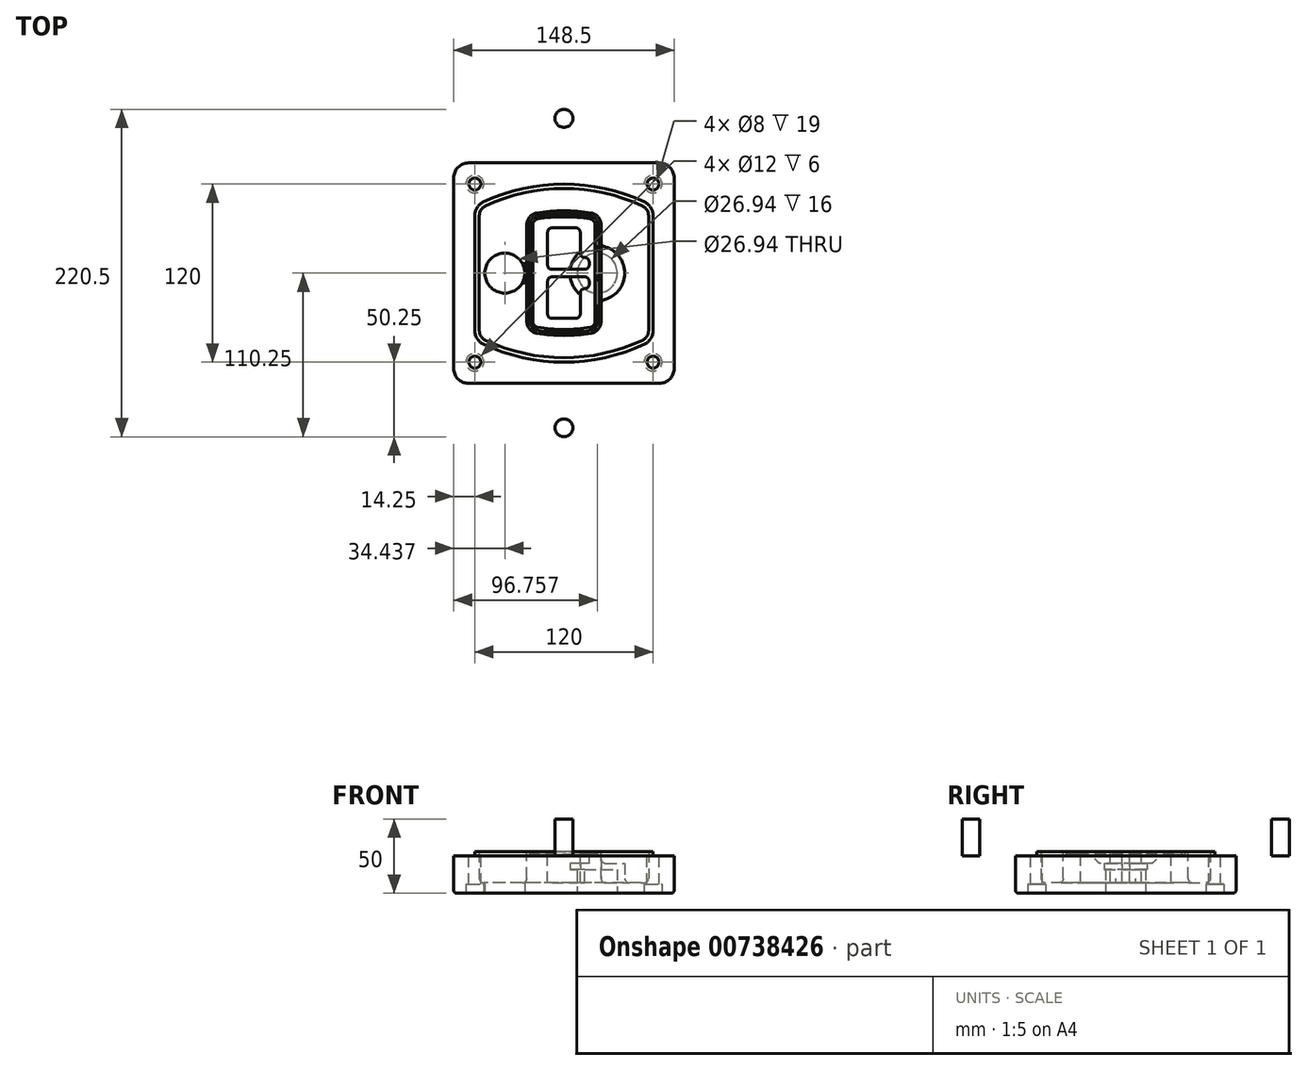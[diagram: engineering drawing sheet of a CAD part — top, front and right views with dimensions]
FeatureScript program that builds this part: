
annotation { "Feature Type Name" : "Feature", "Feature Type Description" : "" }
export const myFeature = defineFeature(function(context is Context, id is Id, definition is map)
    precondition{}
    {
        {
            var Q0;
            Q0=qCreatedBy(makeId("Top.planeOp"),FACE);
            var sketch = newSketch(context, id + "F0", { "sketchPlane" : qUnion([Q0])});
            skPoint(sketch, "E0.rect.middle", {"position": v(0, 0) * mm});
            skLineSegment(sketch, "E1.bottom", {"start": v(-64.25, -74.25) * mm, "end": v(64.25, -74.25) * mm});
            skLineSegment(sketch, "E1.top", {"start": v(-64.25, 74.25) * mm, "end": v(64.25, 74.25) * mm});
            skLineSegment(sketch, "E1.left", {"start": v(-74.25, -64.25) * mm, "end": v(-74.25, 64.25) * mm});
            skLineSegment(sketch, "E1.right", {"start": v(74.25, -64.25) * mm, "end": v(74.25, 64.25) * mm});
            skLineSegment(sketch, "E2", {"start": v(-74.25, 74.25) * mm, "end": v(74.25, -74.25) * mm, "construction": true});
            skLineSegment(sketch, "E3", {"start": v(74.25, 74.25) * mm, "end": v(-74.25, -74.25) * mm, "construction": true});
            skCircle(sketch, "E4", {"center": v(-60, 60) * mm, "radius": 4 * mm});
            skCircle(sketch, "E5", {"center": v(60, 60) * mm, "radius": 4 * mm});
            skCircle(sketch, "E6", {"center": v(60, -60) * mm, "radius": 4 * mm});
            skCircle(sketch, "E7", {"center": v(-60, -60) * mm, "radius": 4 * mm});
            skLineSegment(sketch, "E8", {"start": v(-60, 60) * mm, "end": v(60, 60) * mm, "construction": true});
            skLineSegment(sketch, "E9", {"start": v(60, 60) * mm, "end": v(60, -60) * mm, "construction": true});
            skLineSegment(sketch, "E10", {"start": v(60, -60) * mm, "end": v(-60, -60) * mm, "construction": true});
            skLineSegment(sketch, "E11", {"start": v(-60, -60) * mm, "end": v(-60, 60) * mm, "construction": true});
            skLineSegment(sketch, "E12", {"start": v(-60, 38.83) * mm, "end": v(-60, -38.83) * mm});
            skLineSegment(sketch, "E13", {"start": v(60, 38.83) * mm, "end": v(60, -38.83) * mm});
            skArc(sketch, "E14", {"start": v(54.26, 47.88) * mm, "mid": v(0, 60) * mm, "end": v(-54.26, 47.88) * mm});
            skArc(sketch, "E15", {"start": v(-54.26, -47.88) * mm, "mid": v(0, -60) * mm, "end": v(54.26, -47.88) * mm});
            skLineSegment(sketch, "E16", {"start": v(-60, 0) * mm, "end": v(60, 0) * mm, "construction": true});
            skPoint(sketch, "E17.visualSharp", {"position": v(-60, -45) * mm});
            skArc(sketch, "E17.filletArc", {"start": v(-60, -38.83) * mm, "mid": v(-58.44, -44.2) * mm, "end": v(-54.26, -47.88) * mm});
            skPoint(sketch, "E18.visualSharp", {"position": v(-60, 45) * mm});
            skArc(sketch, "E18.filletArc", {"start": v(-54.26, 47.88) * mm, "mid": v(-58.44, 44.2) * mm, "end": v(-60, 38.83) * mm});
            skPoint(sketch, "E19.visualSharp", {"position": v(60, 45) * mm});
            skArc(sketch, "E19.filletArc", {"start": v(60, 38.83) * mm, "mid": v(58.44, 44.2) * mm, "end": v(54.26, 47.88) * mm});
            skPoint(sketch, "E20.visualSharp", {"position": v(60, -45) * mm});
            skArc(sketch, "E20.filletArc", {"start": v(54.26, -47.88) * mm, "mid": v(58.44, -44.2) * mm, "end": v(60, -38.83) * mm});
            skPoint(sketch, "E21.visualSharp", {"position": v(-74.25, 74.25) * mm});
            skArc(sketch, "E21.filletArc", {"start": v(-64.25, 74.25) * mm, "mid": v(-71.32, 71.32) * mm, "end": v(-74.25, 64.25) * mm});
            skPoint(sketch, "E22.visualSharp", {"position": v(74.25, 74.25) * mm});
            skArc(sketch, "E22.filletArc", {"start": v(74.25, 64.25) * mm, "mid": v(71.32, 71.32) * mm, "end": v(64.25, 74.25) * mm});
            skPoint(sketch, "E23.visualSharp", {"position": v(74.25, -74.25) * mm});
            skArc(sketch, "E23.filletArc", {"start": v(64.25, -74.25) * mm, "mid": v(71.32, -71.32) * mm, "end": v(74.25, -64.25) * mm});
            skPoint(sketch, "E24.visualSharp", {"position": v(-74.25, -74.25) * mm});
            skArc(sketch, "E24.filletArc", {"start": v(-74.25, -64.25) * mm, "mid": v(-71.32, -71.32) * mm, "end": v(-64.25, -74.25) * mm});
            skArc(sketch, "E25.0", {"start": v(57, 38.83) * mm, "mid": v(55.9, 42.58) * mm, "end": v(52.98, 45.17) * mm});
            skLineSegment(sketch, "E25.1", {"start": v(57, 38.83) * mm, "end": v(57, -38.83) * mm});
            skArc(sketch, "E25.2", {"start": v(52.98, -45.17) * mm, "mid": v(55.9, -42.58) * mm, "end": v(57, -38.83) * mm});
            skArc(sketch, "E25.3", {"start": v(-52.98, -45.17) * mm, "mid": v(0, -57) * mm, "end": v(52.98, -45.17) * mm});
            skArc(sketch, "E25.4", {"start": v(-57, -38.83) * mm, "mid": v(-55.9, -42.58) * mm, "end": v(-52.98, -45.17) * mm});
            skArc(sketch, "E25.5", {"start": v(52.98, 45.17) * mm, "mid": v(0, 57) * mm, "end": v(-52.98, 45.17) * mm});
            skLineSegment(sketch, "E25.6", {"start": v(-57, 38.83) * mm, "end": v(-57, -38.83) * mm});
            skArc(sketch, "E25.7", {"start": v(-52.98, 45.17) * mm, "mid": v(-55.9, 42.58) * mm, "end": v(-57, 38.83) * mm});
            skArc(sketch, "E26.0", {"start": v(-55.96, 51.5) * mm, "mid": v(-61.82, 46.33) * mm, "end": v(-64, 38.83) * mm});
            skArc(sketch, "E26.1", {"start": v(55.96, 51.5) * mm, "mid": v(0, 64) * mm, "end": v(-55.96, 51.5) * mm});
            skArc(sketch, "E26.2", {"start": v(64, 38.83) * mm, "mid": v(61.82, 46.33) * mm, "end": v(55.96, 51.5) * mm});
            skLineSegment(sketch, "E26.3", {"start": v(64, 38.83) * mm, "end": v(64, -38.83) * mm});
            skArc(sketch, "E26.4", {"start": v(55.96, -51.5) * mm, "mid": v(61.82, -46.33) * mm, "end": v(64, -38.83) * mm});
            skLineSegment(sketch, "E26.5", {"start": v(-64, 38.83) * mm, "end": v(-64, -38.83) * mm});
            skArc(sketch, "E26.6", {"start": v(-55.96, -51.5) * mm, "mid": v(0, -64) * mm, "end": v(55.96, -51.5) * mm});
            skArc(sketch, "E26.7", {"start": v(-64, -38.83) * mm, "mid": v(-61.82, -46.33) * mm, "end": v(-55.96, -51.5) * mm});
            skSolve(sketch);
        }
        {
            var Q0;
            Q0=makeQuery(id+"F0.imprint","IMPRINT",FACE,{"disambiguationData":[TD([[makeQuery(id+"F0.imprint","IMPRINT",EDGE,{"derivedFrom":sQuery(id+"F0.wireOp",EDGE,"E1.bottom")}),1.0]])]});
            var Q1;
            Q1=makeQuery(id+"F0.imprint","IMPRINT",FACE,{"disambiguationData":[TD([[makeQuery(id+"F0.imprint","IMPRINT",EDGE,{"derivedFrom":sQuery(id+"F0.wireOp",EDGE,"E12")}),1.0]])]});
            var Q2;
            Q2=makeQuery(id+"F0.imprint","IMPRINT",FACE,{"disambiguationData":[TD([[makeQuery(id+"F0.imprint","IMPRINT",EDGE,{"derivedFrom":sQuery(id+"F0.wireOp",EDGE,"E25.0")}),1.0]])]});
            var Q3;
            Q3=makeQuery(id+"F0.imprint","IMPRINT",FACE,{"disambiguationData":[TD([[makeQuery(id+"F0.imprint","IMPRINT",EDGE,{"derivedFrom":sQuery(id+"F0.wireOp",EDGE,"E12")}),-1.0]])]});
            extrude(context, id + "F1", {"entities" : qUnion([Q0, Q1, Q2, Q3]), "oppositeDirection" : true, "depth" : 25 * mm});
        }
        {
            var Q0;
            Q0=makeQuery(id+"F0.imprint","IMPRINT",FACE,{"disambiguationData":[TD([[makeQuery(id+"F0.imprint","IMPRINT",EDGE,{"derivedFrom":sQuery(id+"F0.wireOp",EDGE,"E12")}),1.0]])]});
            extrude(context, id + "F2", {"entities" : qUnion([Q0]), "operationType" : NewBodyOperationType.ADD, "depth" : 3 * mm});
        }
        {
            var Q0;
            Q0=makeQuery(id+"F0.imprint","IMPRINT",FACE,{"disambiguationData":[TD([[makeQuery(id+"F0.imprint","IMPRINT",EDGE,{"derivedFrom":sQuery(id+"F0.wireOp",EDGE,"E25.0")}),1.0]])]});
            extrude(context, id + "F3", {"entities" : qUnion([Q0]), "operationType" : NewBodyOperationType.REMOVE, "oppositeDirection" : true, "depth" : 18 * mm});
        }
        {
            var Q0;
            Q0=makeQuery(id+"F2.opExtrude","CAP_FACE",FACE,{"disambiguationData":[OSD([sQuery(id+"F0.wireOp",EDGE,"E12"),sQuery(id+"F0.wireOp",EDGE,"E13"),sQuery(id+"F0.wireOp",EDGE,"E14"),sQuery(id+"F0.wireOp",EDGE,"E15"),sQuery(id+"F0.wireOp",EDGE,"E17.filletArc"),sQuery(id+"F0.wireOp",EDGE,"E18.filletArc"),sQuery(id+"F0.wireOp",EDGE,"E19.filletArc"),sQuery(id+"F0.wireOp",EDGE,"E20.filletArc"),sQuery(id+"F0.wireOp",EDGE,"E25.0"),sQuery(id+"F0.wireOp",EDGE,"E25.1"),sQuery(id+"F0.wireOp",EDGE,"E25.2"),sQuery(id+"F0.wireOp",EDGE,"E25.3"),sQuery(id+"F0.wireOp",EDGE,"E25.4"),sQuery(id+"F0.wireOp",EDGE,"E25.5"),sQuery(id+"F0.wireOp",EDGE,"E25.6"),sQuery(id+"F0.wireOp",EDGE,"E25.7")])],"isStart":false});
            var sketch = newSketch(context, id + "F4", { "sketchPlane" : qUnion([Q0])});
            skArc(sketch, "E27.0", {"start": v(-18.34, -40.45) * mm, "mid": v(0, -42) * mm, "end": v(18.34, -40.45) * mm});
            skArc(sketch, "E28.0", {"start": v(18.34, 40.45) * mm, "mid": v(0, 42) * mm, "end": v(-18.34, 40.45) * mm});
            skLineSegment(sketch, "E29", {"start": v(-25, 32.57) * mm, "end": v(-25, -32.57) * mm});
            skLineSegment(sketch, "E30", {"start": v(25, 32.57) * mm, "end": v(25, -32.57) * mm});
            skLineSegment(sketch, "E31", {"start": v(-25, 39.1) * mm, "end": v(25, 39.1) * mm, "construction": true});
            skLineSegment(sketch, "E32", {"start": v(-25, -39.1) * mm, "end": v(25, -39.1) * mm, "construction": true});
            skPoint(sketch, "E33.visualSharp", {"position": v(-25, 39.1) * mm});
            skArc(sketch, "E33.filletArc", {"start": v(-18.34, 40.45) * mm, "mid": v(-23.11, 37.73) * mm, "end": v(-25, 32.57) * mm});
            skPoint(sketch, "E34.visualSharp", {"position": v(25, 39.1) * mm});
            skArc(sketch, "E34.filletArc", {"start": v(25, 32.57) * mm, "mid": v(23.11, 37.73) * mm, "end": v(18.34, 40.45) * mm});
            skPoint(sketch, "E35.visualSharp", {"position": v(25, -39.1) * mm});
            skArc(sketch, "E35.filletArc", {"start": v(18.34, -40.45) * mm, "mid": v(23.11, -37.73) * mm, "end": v(25, -32.57) * mm});
            skPoint(sketch, "E36.visualSharp", {"position": v(-25, -39.1) * mm});
            skArc(sketch, "E36.filletArc", {"start": v(-25, -32.57) * mm, "mid": v(-23.11, -37.73) * mm, "end": v(-18.34, -40.45) * mm});
            skArc(sketch, "E37.0", {"start": v(52.98, 45.17) * mm, "mid": v(0, 57) * mm, "end": v(-52.98, 45.17) * mm});
            skArc(sketch, "E37.1", {"start": v(-52.98, 45.17) * mm, "mid": v(-55.9, 42.58) * mm, "end": v(-57, 38.83) * mm});
            skLineSegment(sketch, "E37.2", {"start": v(-57, 38.83) * mm, "end": v(-57, -38.83) * mm});
            skArc(sketch, "E37.3", {"start": v(-57, -38.83) * mm, "mid": v(-55.9, -42.58) * mm, "end": v(-52.98, -45.17) * mm});
            skArc(sketch, "E37.4", {"start": v(-52.98, -45.17) * mm, "mid": v(0, -57) * mm, "end": v(52.98, -45.17) * mm});
            skArc(sketch, "E37.5", {"start": v(52.98, -45.17) * mm, "mid": v(55.9, -42.58) * mm, "end": v(57, -38.83) * mm});
            skLineSegment(sketch, "E37.6", {"start": v(57, 38.83) * mm, "end": v(57, -38.83) * mm});
            skArc(sketch, "E37.7", {"start": v(57, 38.83) * mm, "mid": v(55.9, 42.58) * mm, "end": v(52.98, 45.17) * mm});
            skLineSegment(sketch, "E38.0", {"start": v(23, 32.57) * mm, "end": v(23, -32.57) * mm});
            skArc(sketch, "E38.1", {"start": v(18, -38.48) * mm, "mid": v(21.58, -36.44) * mm, "end": v(23, -32.57) * mm});
            skArc(sketch, "E38.2", {"start": v(-18, -38.48) * mm, "mid": v(0, -40) * mm, "end": v(18, -38.48) * mm});
            skArc(sketch, "E38.3", {"start": v(-23, -32.57) * mm, "mid": v(-21.58, -36.44) * mm, "end": v(-18, -38.48) * mm});
            skLineSegment(sketch, "E38.4", {"start": v(-23, 32.57) * mm, "end": v(-23, -32.57) * mm});
            skArc(sketch, "E38.5", {"start": v(23, 32.57) * mm, "mid": v(21.58, 36.44) * mm, "end": v(18, 38.48) * mm});
            skArc(sketch, "E38.6", {"start": v(-18, 38.48) * mm, "mid": v(-21.58, 36.44) * mm, "end": v(-23, 32.57) * mm});
            skArc(sketch, "E38.7", {"start": v(18, 38.48) * mm, "mid": v(0, 40) * mm, "end": v(-18, 38.48) * mm});
            skArc(sketch, "E39.0", {"start": v(21, 32.57) * mm, "mid": v(20.06, 35.15) * mm, "end": v(17.67, 36.5) * mm});
            skLineSegment(sketch, "E39.1", {"start": v(21, 32.57) * mm, "end": v(21, -32.57) * mm});
            skArc(sketch, "E39.2", {"start": v(17.67, -36.5) * mm, "mid": v(20.06, -35.15) * mm, "end": v(21, -32.57) * mm});
            skArc(sketch, "E39.3", {"start": v(-17.67, -36.5) * mm, "mid": v(0, -38) * mm, "end": v(17.67, -36.5) * mm});
            skArc(sketch, "E39.4", {"start": v(-21, -32.57) * mm, "mid": v(-20.06, -35.15) * mm, "end": v(-17.67, -36.5) * mm});
            skArc(sketch, "E39.5", {"start": v(17.67, 36.5) * mm, "mid": v(0, 38) * mm, "end": v(-17.67, 36.5) * mm});
            skLineSegment(sketch, "E39.6", {"start": v(-21, 32.57) * mm, "end": v(-21, -32.57) * mm});
            skArc(sketch, "E39.7", {"start": v(-17.67, 36.5) * mm, "mid": v(-20.06, 35.15) * mm, "end": v(-21, 32.57) * mm});
            skLineSegment(sketch, "E40", {"start": v(-25, 0) * mm, "end": v(25, 0) * mm, "construction": true});
            skLineSegment(sketch, "E41", {"start": v(-11, 5.5) * mm, "end": v(-11, 27.5) * mm});
            skLineSegment(sketch, "E42", {"start": v(-8, 30.5) * mm, "end": v(8, 30.5) * mm});
            skLineSegment(sketch, "E43", {"start": v(11, 27.5) * mm, "end": v(11, 13.5) * mm});
            skLineSegment(sketch, "E44", {"start": v(14, 10.5) * mm, "end": v(14, 10.5) * mm});
            skLineSegment(sketch, "E45", {"start": v(17, 7.5) * mm, "end": v(17, 5.5) * mm});
            skLineSegment(sketch, "E46", {"start": v(14, 2.5) * mm, "end": v(-8, 2.5) * mm});
            skPoint(sketch, "E47.visualSharp", {"position": v(-11, 30.5) * mm});
            skArc(sketch, "E47.filletArc", {"start": v(-8, 30.5) * mm, "mid": v(-10.12, 29.62) * mm, "end": v(-11, 27.5) * mm});
            skPoint(sketch, "E48.visualSharp", {"position": v(11, 30.5) * mm});
            skArc(sketch, "E48.filletArc", {"start": v(11, 27.5) * mm, "mid": v(10.12, 29.62) * mm, "end": v(8, 30.5) * mm});
            skPoint(sketch, "E49.visualSharp", {"position": v(11, 10.5) * mm});
            skArc(sketch, "E49.filletArc", {"start": v(11, 13.5) * mm, "mid": v(11.88, 11.38) * mm, "end": v(14, 10.5) * mm});
            skPoint(sketch, "E50.visualSharp", {"position": v(17, 10.5) * mm});
            skArc(sketch, "E50.filletArc", {"start": v(17, 7.5) * mm, "mid": v(16.12, 9.62) * mm, "end": v(14, 10.5) * mm});
            skPoint(sketch, "E51.visualSharp", {"position": v(17, 2.5) * mm});
            skArc(sketch, "E51.filletArc", {"start": v(14, 2.5) * mm, "mid": v(16.12, 3.38) * mm, "end": v(17, 5.5) * mm});
            skPoint(sketch, "E52.visualSharp", {"position": v(-11, 2.5) * mm});
            skArc(sketch, "E52.filletArc", {"start": v(-11, 5.5) * mm, "mid": v(-10.12, 3.38) * mm, "end": v(-8, 2.5) * mm});
            skLineSegment(sketch, "E53.0.MirrorCS", {"start": v(14, -2.5) * mm, "end": v(-8, -2.5) * mm});
            skArc(sketch, "E54.0.MirrorCS", {"start": v(-11, -5.5) * mm, "mid": v(-10.12, -3.38) * mm, "end": v(-8, -2.5) * mm});
            skLineSegment(sketch, "E55.0.MirrorCS", {"start": v(-11, -5.5) * mm, "end": v(-11, -27.5) * mm});
            skArc(sketch, "E56.0.MirrorCS", {"start": v(-8, -30.5) * mm, "mid": v(-10.12, -29.62) * mm, "end": v(-11, -27.5) * mm});
            skLineSegment(sketch, "E57.0.MirrorCS", {"start": v(-8, -30.5) * mm, "end": v(8, -30.5) * mm});
            skArc(sketch, "E58.0.MirrorCS", {"start": v(11, -27.5) * mm, "mid": v(10.12, -29.62) * mm, "end": v(8, -30.5) * mm});
            skLineSegment(sketch, "E59.0.MirrorCS", {"start": v(11, -27.5) * mm, "end": v(11, -13.5) * mm});
            skArc(sketch, "E60.0.MirrorCS", {"start": v(11, -13.5) * mm, "mid": v(11.88, -11.38) * mm, "end": v(14, -10.5) * mm});
            skArc(sketch, "E61.0.MirrorCS", {"start": v(17, -7.5) * mm, "mid": v(16.12, -9.62) * mm, "end": v(14, -10.5) * mm});
            skLineSegment(sketch, "E62.0.MirrorCS", {"start": v(17, -7.5) * mm, "end": v(17, -5.5) * mm});
            skArc(sketch, "E63.0.MirrorCS", {"start": v(14, -2.5) * mm, "mid": v(16.12, -3.38) * mm, "end": v(17, -5.5) * mm});
            skSolve(sketch);
        }
        {
            var Q0;
            Q0=makeQuery(id+"F4.imprint","IMPRINT",FACE,{"disambiguationData":[TD([[makeQuery(id+"F4.imprint","IMPRINT",EDGE,{"derivedFrom":sQuery(id+"F4.wireOp",EDGE,"E27.0")}),1.0]])]});
            var Q1;
            Q1=makeQuery(id+"F4.imprint","IMPRINT",FACE,{"disambiguationData":[TD([[makeQuery(id+"F4.imprint","IMPRINT",EDGE,{"derivedFrom":sQuery(id+"F4.wireOp",EDGE,"E38.0")}),-1.0]])]});
            var Q2;
            Q2=makeQuery(id+"F4.imprint","IMPRINT",FACE,{"disambiguationData":[TD([[makeQuery(id+"F4.imprint","IMPRINT",EDGE,{"derivedFrom":sQuery(id+"F4.wireOp",EDGE,"E39.0")}),1.0]])]});
            extrude(context, id + "F5", {"entities" : qUnion([Q0, Q1, Q2]), "operationType" : NewBodyOperationType.ADD, "endBound" : BoundingType.UP_TO_NEXT, "oppositeDirection" : true, "depth" : 25 * mm});
        }
        {
            var Q0;
            Q0=makeQuery(id+"F4.imprint","IMPRINT",FACE,{"disambiguationData":[TD([[makeQuery(id+"F4.imprint","IMPRINT",EDGE,{"derivedFrom":sQuery(id+"F4.wireOp",EDGE,"E38.0")}),-1.0]])]});
            extrude(context, id + "F6", {"entities" : qUnion([Q0]), "operationType" : NewBodyOperationType.REMOVE, "oppositeDirection" : true, "depth" : 2 * mm});
        }
        {
            var Q0;
            Q0=makeQuery(id+"F1.opExtrude","CAP_FACE",FACE,{"disambiguationData":[OSD([sQuery(id+"F0.wireOp",EDGE,"E1.bottom"),sQuery(id+"F0.wireOp",EDGE,"E1.top"),sQuery(id+"F0.wireOp",EDGE,"E1.left"),sQuery(id+"F0.wireOp",EDGE,"E1.right"),sQuery(id+"F0.wireOp",EDGE,"E4"),sQuery(id+"F0.wireOp",EDGE,"E5"),sQuery(id+"F0.wireOp",EDGE,"E6"),sQuery(id+"F0.wireOp",EDGE,"E7"),sQuery(id+"F0.wireOp",EDGE,"E21.filletArc"),sQuery(id+"F0.wireOp",EDGE,"E22.filletArc"),sQuery(id+"F0.wireOp",EDGE,"E23.filletArc"),sQuery(id+"F0.wireOp",EDGE,"E24.filletArc")])],"isStart":false});
            var sketch = newSketch(context, id + "F7", { "sketchPlane" : qUnion([Q0])});
            skCircle(sketch, "E64", {"center": v(22.5, 0) * mm, "radius": 13.47 * mm});
            skCircle(sketch, "E65", {"center": v(-39.81, 0) * mm, "radius": 13.47 * mm});
            skLineSegment(sketch, "E66", {"start": v(74.25, 0) * mm, "end": v(-74.25, 0) * mm});
            skCircle(sketch, "E67", {"center": v(22.5, 0) * mm, "radius": 18.47 * mm});
            skCircle(sketch, "E68", {"center": v(60, -60) * mm, "radius": 6 * mm});
            skCircle(sketch, "E69", {"center": v(-60, -60) * mm, "radius": 6 * mm});
            skCircle(sketch, "E70", {"center": v(-60, 60) * mm, "radius": 6 * mm});
            skCircle(sketch, "E71", {"center": v(60, 60) * mm, "radius": 6 * mm});
            skSolve(sketch);
        }
        {
            var Q0;
            {var subQ1=sQuery(id+"F7.wireOp",EDGE,"E66");var subQ4=sQuery(id+"F7.wireOp",EDGE,"E64");var subQ6=makeQuery(id+"F7.imprint","INTERSECT",VERTEX,{"disambiguationData":[OD(0.0)],"derivedFrom":[subQ4,subQ1]});Q0=makeQuery(id+"F7.imprint","IMPRINT",FACE,{"disambiguationData":[TD([[makeQuery(id+"F7.imprint","IMPRINT",EDGE,{"disambiguationData":[TD([[subQ6,-1.0]])],"derivedFrom":subQ4}),-1.0]])]});}
            var Q1;
            {var subQ0=sQuery(id+"F7.wireOp",EDGE,"E66");var subQ1=sQuery(id+"F7.wireOp",EDGE,"E64");var subQ3=makeQuery(id+"F7.imprint","INTERSECT",VERTEX,{"disambiguationData":[OD(0.0)],"derivedFrom":[subQ1,subQ0]});Q1=makeQuery(id+"F7.imprint","IMPRINT",FACE,{"disambiguationData":[TD([[makeQuery(id+"F7.imprint","IMPRINT",EDGE,{"disambiguationData":[TD([[subQ3,-1.0]])],"derivedFrom":subQ1}),1.0]])]});}
            var Q2;
            {var subQ0=sQuery(id+"F7.wireOp",EDGE,"E66");var subQ1=sQuery(id+"F7.wireOp",EDGE,"E64");var subQ3=makeQuery(id+"F7.imprint","INTERSECT",VERTEX,{"disambiguationData":[OD(0.0)],"derivedFrom":[subQ1,subQ0]});Q2=makeQuery(id+"F7.imprint","IMPRINT",FACE,{"disambiguationData":[TD([[makeQuery(id+"F7.imprint","IMPRINT",EDGE,{"disambiguationData":[TD([[subQ3,1.0]])],"derivedFrom":subQ1}),1.0]])]});}
            var Q3;
            {var subQ1=sQuery(id+"F7.wireOp",EDGE,"E66");var subQ4=sQuery(id+"F7.wireOp",EDGE,"E64");var subQ6=makeQuery(id+"F7.imprint","INTERSECT",VERTEX,{"disambiguationData":[OD(0.0)],"derivedFrom":[subQ4,subQ1]});Q3=makeQuery(id+"F7.imprint","IMPRINT",FACE,{"disambiguationData":[TD([[makeQuery(id+"F7.imprint","IMPRINT",EDGE,{"disambiguationData":[TD([[subQ6,1.0]])],"derivedFrom":subQ4}),-1.0]])]});}
            extrude(context, id + "F8", {"entities" : qUnion([Q0, Q1, Q2, Q3]), "operationType" : NewBodyOperationType.ADD, "oppositeDirection" : true, "depth" : 20 * mm});
        }
        {
            var Q0;
            {var subQ0=sQuery(id+"F7.wireOp",EDGE,"E66");var subQ1=sQuery(id+"F7.wireOp",EDGE,"E64");var subQ3=makeQuery(id+"F7.imprint","INTERSECT",VERTEX,{"disambiguationData":[OD(0.0)],"derivedFrom":[subQ1,subQ0]});Q0=makeQuery(id+"F7.imprint","IMPRINT",FACE,{"disambiguationData":[TD([[makeQuery(id+"F7.imprint","IMPRINT",EDGE,{"disambiguationData":[TD([[subQ3,-1.0]])],"derivedFrom":subQ1}),1.0]])]});}
            var Q1;
            {var subQ0=sQuery(id+"F7.wireOp",EDGE,"E66");var subQ1=sQuery(id+"F7.wireOp",EDGE,"E64");var subQ3=makeQuery(id+"F7.imprint","INTERSECT",VERTEX,{"disambiguationData":[OD(0.0)],"derivedFrom":[subQ1,subQ0]});Q1=makeQuery(id+"F7.imprint","IMPRINT",FACE,{"disambiguationData":[TD([[makeQuery(id+"F7.imprint","IMPRINT",EDGE,{"disambiguationData":[TD([[subQ3,1.0]])],"derivedFrom":subQ1}),1.0]])]});}
            extrude(context, id + "F9", {"entities" : qUnion([Q0, Q1]), "operationType" : NewBodyOperationType.REMOVE, "oppositeDirection" : true, "depth" : 16 * mm});
        }
        {
            var Q0;
            {var subQ0=sQuery(id+"F7.wireOp",EDGE,"E66");var subQ1=sQuery(id+"F7.wireOp",EDGE,"E65");var subQ3=makeQuery(id+"F7.imprint","INTERSECT",VERTEX,{"disambiguationData":[OD(0.0)],"derivedFrom":[subQ1,subQ0]});Q0=makeQuery(id+"F7.imprint","IMPRINT",FACE,{"disambiguationData":[TD([[makeQuery(id+"F7.imprint","IMPRINT",EDGE,{"disambiguationData":[TD([[subQ3,-1.0]])],"derivedFrom":subQ1}),1.0]])]});}
            var Q1;
            {var subQ0=sQuery(id+"F7.wireOp",EDGE,"E66");var subQ1=sQuery(id+"F7.wireOp",EDGE,"E65");var subQ3=makeQuery(id+"F7.imprint","INTERSECT",VERTEX,{"disambiguationData":[OD(0.0)],"derivedFrom":[subQ1,subQ0]});Q1=makeQuery(id+"F7.imprint","IMPRINT",FACE,{"disambiguationData":[TD([[makeQuery(id+"F7.imprint","IMPRINT",EDGE,{"disambiguationData":[TD([[subQ3,1.0]])],"derivedFrom":subQ1}),1.0]])]});}
            extrude(context, id + "F10", {"entities" : qUnion([Q0, Q1]), "operationType" : NewBodyOperationType.REMOVE, "oppositeDirection" : true, "depth" : 25 * mm});
        }
        {
            var Q0;
            Q0=makeQuery(id+"F7.imprint","IMPRINT",FACE,{"disambiguationData":[TD([[makeQuery(id+"F7.imprint","IMPRINT",EDGE,{"derivedFrom":sQuery(id+"F7.wireOp",EDGE,"E68")}),1.0]])]});
            var Q1;
            Q1=makeQuery(id+"F7.imprint","IMPRINT",FACE,{"disambiguationData":[TD([[makeQuery(id+"F7.imprint","IMPRINT",EDGE,{"derivedFrom":makeQuery(id+"F1.opExtrude","CAP_EDGE",EDGE,{"disambiguationData":[OSD([sQuery(id+"F0.wireOp",EDGE,"E5")])],"isStart":false})}),-1.0]])]});
            var Q2;
            Q2=makeQuery(id+"F7.imprint","IMPRINT",FACE,{"disambiguationData":[TD([[makeQuery(id+"F7.imprint","IMPRINT",EDGE,{"derivedFrom":sQuery(id+"F7.wireOp",EDGE,"E69")}),1.0]])]});
            var Q3;
            Q3=makeQuery(id+"F7.imprint","IMPRINT",FACE,{"disambiguationData":[TD([[makeQuery(id+"F7.imprint","IMPRINT",EDGE,{"derivedFrom":makeQuery(id+"F1.opExtrude","CAP_EDGE",EDGE,{"disambiguationData":[OSD([sQuery(id+"F0.wireOp",EDGE,"E4")])],"isStart":false})}),-1.0]])]});
            var Q4;
            Q4=makeQuery(id+"F7.imprint","IMPRINT",FACE,{"disambiguationData":[TD([[makeQuery(id+"F7.imprint","IMPRINT",EDGE,{"derivedFrom":sQuery(id+"F7.wireOp",EDGE,"E70")}),1.0]])]});
            var Q5;
            Q5=makeQuery(id+"F7.imprint","IMPRINT",FACE,{"disambiguationData":[TD([[makeQuery(id+"F7.imprint","IMPRINT",EDGE,{"derivedFrom":makeQuery(id+"F1.opExtrude","CAP_EDGE",EDGE,{"disambiguationData":[OSD([sQuery(id+"F0.wireOp",EDGE,"E7")])],"isStart":false})}),-1.0]])]});
            var Q6;
            Q6=makeQuery(id+"F7.imprint","IMPRINT",FACE,{"disambiguationData":[TD([[makeQuery(id+"F7.imprint","IMPRINT",EDGE,{"derivedFrom":sQuery(id+"F7.wireOp",EDGE,"E71")}),1.0]])]});
            var Q7;
            Q7=makeQuery(id+"F7.imprint","IMPRINT",FACE,{"disambiguationData":[TD([[makeQuery(id+"F7.imprint","IMPRINT",EDGE,{"derivedFrom":makeQuery(id+"F1.opExtrude","CAP_EDGE",EDGE,{"disambiguationData":[OSD([sQuery(id+"F0.wireOp",EDGE,"E6")])],"isStart":false})}),-1.0]])]});
            extrude(context, id + "F11", {"entities" : qUnion([Q0, Q1, Q2, Q3, Q4, Q5, Q6, Q7]), "operationType" : NewBodyOperationType.REMOVE, "oppositeDirection" : true, "depth" : 6 * mm});
        }
        {
            var Q0;
            Q0=makeQuery(id+"F9.boolean.opBoolean","COPY",FACE,{"derivedFrom":makeQuery(id+"F9.opExtrude","CAP_FACE",FACE,{"disambiguationData":[OSD([sQuery(id+"F7.wireOp",EDGE,"E64")])],"isStart":false})});
            var sketch = newSketch(context, id + "F12", { "sketchPlane" : qUnion([Q0])});
            skArc(sketch, "E72.0", {"start": v(11, 14.45) * mm, "mid": v(6.45, 9.13) * mm, "end": v(4.2, 2.5) * mm});
            skArc(sketch, "E72.1", {"start": v(4.2, -2.5) * mm, "mid": v(6.45, -9.13) * mm, "end": v(11, -14.45) * mm});
            skLineSegment(sketch, "E73", {"start": v(4.2, -2.5) * mm, "end": v(14, -2.5) * mm});
            skLineSegment(sketch, "E74.0", {"start": v(14, 2.5) * mm, "end": v(4.2, 2.5) * mm});
            skArc(sketch, "E74.1", {"start": v(14, 2.5) * mm, "mid": v(16.12, 3.38) * mm, "end": v(17, 5.5) * mm});
            skLineSegment(sketch, "E74.2", {"start": v(17, 7.5) * mm, "end": v(17, 5.5) * mm});
            skArc(sketch, "E74.3", {"start": v(17, 7.5) * mm, "mid": v(16.12, 9.62) * mm, "end": v(14, 10.5) * mm});
            skArc(sketch, "E74.4", {"start": v(11, 13.5) * mm, "mid": v(11.88, 11.38) * mm, "end": v(14, 10.5) * mm});
            skLineSegment(sketch, "E74.5", {"start": v(11, 14.45) * mm, "end": v(11, 13.5) * mm});
            skLineSegment(sketch, "E74.7", {"start": v(14, -2.5) * mm, "end": v(4.2, -2.5) * mm});
            skArc(sketch, "E74.8", {"start": v(14, -2.5) * mm, "mid": v(16.12, -3.38) * mm, "end": v(17, -5.5) * mm});
            skLineSegment(sketch, "E74.9", {"start": v(17, -7.5) * mm, "end": v(17, -5.5) * mm});
            skArc(sketch, "E74.10", {"start": v(17, -7.5) * mm, "mid": v(16.12, -9.62) * mm, "end": v(14, -10.5) * mm});
            skArc(sketch, "E74.11", {"start": v(11, -13.5) * mm, "mid": v(11.88, -11.38) * mm, "end": v(14, -10.5) * mm});
            skLineSegment(sketch, "E74.12", {"start": v(11, -14.45) * mm, "end": v(11, -13.5) * mm});
            skPoint(sketch, "E75.orphan", {"position": v(11, -27.5) * mm});
            skPoint(sketch, "E76.orphan", {"position": v(-8, -2.5) * mm});
            skPoint(sketch, "E77.orphan", {"position": v(-8, 2.5) * mm});
            skPoint(sketch, "E78.orphan", {"position": v(11, 27.5) * mm});
            skSolve(sketch);
        }
        {
            var Q0;
            {var subQ7=sQuery(id+"F12.wireOp",EDGE,"E72.0");var subQ14=sQuery(id+"F12.wireOp",EDGE,"E72.1");var subQ16=sQuery(id+"F12.wireOp",EDGE,"E74.1");var subQ18=sQuery(id+"F12.wireOp",EDGE,"E74.8");Q0=qUnion([makeQuery(id+"F12.imprint","IMPRINT",FACE,{"disambiguationData":[TD([[makeQuery(id+"F12.imprint","IMPRINT",EDGE,{"derivedFrom":subQ7}),1.0]])]}),makeQuery(id+"F12.imprint","IMPRINT",FACE,{"disambiguationData":[TD([[makeQuery(id+"F12.imprint","IMPRINT",EDGE,{"derivedFrom":subQ14}),1.0]])]}),makeQuery(id+"F12.imprint","IMPRINT",FACE,{"disambiguationData":[TD([[makeQuery(id+"F12.imprint","IMPRINT",EDGE,{"derivedFrom":subQ16}),1.0]])]}),makeQuery(id+"F12.imprint","IMPRINT",FACE,{"disambiguationData":[TD([[makeQuery(id+"F12.imprint","IMPRINT",EDGE,{"derivedFrom":subQ18}),-1.0]])]})]);}
            var Q1;
            Q1=makeQuery(id+"F5.boolean.opBoolean","SPLIT",FACE,{"disambiguationData":[TD([makeQuery(id+"F5.opExtrude","SWEPT_FACE",FACE,{"disambiguationData":[OSD([sQuery(id+"F4.wireOp",EDGE,"E41")])]})])],"derivedFrom":makeQuery(id+"F3.boolean.opBoolean","COPY",FACE,{"derivedFrom":makeQuery(id+"F3.opExtrude","CAP_FACE",FACE,{"disambiguationData":[OSD([sQuery(id+"F0.wireOp",EDGE,"E25.0"),sQuery(id+"F0.wireOp",EDGE,"E25.1"),sQuery(id+"F0.wireOp",EDGE,"E25.2"),sQuery(id+"F0.wireOp",EDGE,"E25.3"),sQuery(id+"F0.wireOp",EDGE,"E25.4"),sQuery(id+"F0.wireOp",EDGE,"E25.5"),sQuery(id+"F0.wireOp",EDGE,"E25.6"),sQuery(id+"F0.wireOp",EDGE,"E25.7")])],"isStart":false})})});
            extrude(context, id + "F13", {"entities" : qUnion([Q0]), "operationType" : NewBodyOperationType.REMOVE, "endBound" : BoundingType.UP_TO_SURFACE, "endBoundEntityFace" : qUnion([Q1]), "depth" : 25 * mm});
        }
        {
            var Q0;
            Q0=makeQuery(id+"F3.boolean.opBoolean","COPY",EDGE,{"derivedFrom":makeQuery(id+"F3.opExtrude","CAP_EDGE",EDGE,{"disambiguationData":[OSD([sQuery(id+"F0.wireOp",EDGE,"E25.6")])],"isStart":false})});
            var Q1;
            Q1=makeQuery(id+"F8.boolean.opBoolean","INTERSECT",EDGE,{"derivedFrom":[makeQuery(id+"F5.opExtrude","SWEPT_FACE",FACE,{"disambiguationData":[OSD([sQuery(id+"F4.wireOp",EDGE,"E30")])]}),makeQuery(id+"F8.opExtrude","CAP_FACE",FACE,{"disambiguationData":[OSD([sQuery(id+"F7.wireOp",EDGE,"E67")])],"isStart":false})]});
            var Q2;
            Q2=makeQuery(id+"F8.boolean.opBoolean","INTERSECT",EDGE,{"disambiguationData":[OD(1.0)],"derivedFrom":[makeQuery(id+"F5.opExtrude","SWEPT_FACE",FACE,{"disambiguationData":[OSD([sQuery(id+"F4.wireOp",EDGE,"E30")])]}),makeQuery(id+"F8.opExtrude","SWEPT_FACE",FACE,{"disambiguationData":[OSD([sQuery(id+"F7.wireOp",EDGE,"E67")])]})]});
            var Q3;
            {var subQ0=sQuery(id+"F4.wireOp",EDGE,"E30");Q3=makeQuery(id+"F8.boolean.opBoolean","SPLIT",EDGE,{"disambiguationData":[TD([makeQuery(id+"F5.opExtrude","SWEPT_FACE",FACE,{"disambiguationData":[OSD([sQuery(id+"F4.wireOp",EDGE,"E35.filletArc")])]})])],"derivedFrom":makeQuery(id+"F5.opExtrude","CAP_EDGE",EDGE,{"disambiguationData":[OSD([subQ0])],"isStart":false})});}
            var Q4;
            {var subQ0=sQuery(id+"F0.wireOp",EDGE,"E25.7");var subQ1=sQuery(id+"F0.wireOp",EDGE,"E25.1");var subQ2=sQuery(id+"F0.wireOp",EDGE,"E25.6");var subQ3=sQuery(id+"F0.wireOp",EDGE,"E25.5");var subQ4=sQuery(id+"F0.wireOp",EDGE,"E25.4");var subQ5=sQuery(id+"F0.wireOp",EDGE,"E25.0");var subQ6=sQuery(id+"F0.wireOp",EDGE,"E25.2");var subQ7=sQuery(id+"F0.wireOp",EDGE,"E25.3");Q4=makeQuery(id+"F8.boolean.opBoolean","INTERSECT",EDGE,{"derivedFrom":[makeQuery(id+"F5.boolean.opBoolean","SPLIT",FACE,{"disambiguationData":[TD([makeQuery(id+"F2.opExtrude","SWEPT_FACE",FACE,{"disambiguationData":[OSD([subQ5])]})])],"derivedFrom":makeQuery(id+"F3.boolean.opBoolean","COPY",FACE,{"derivedFrom":makeQuery(id+"F3.opExtrude","CAP_FACE",FACE,{"disambiguationData":[OSD([subQ5,subQ1,subQ6,subQ7,subQ4,subQ3,subQ2,subQ0])],"isStart":false})})}),makeQuery(id+"F8.opExtrude","SWEPT_FACE",FACE,{"disambiguationData":[OSD([sQuery(id+"F7.wireOp",EDGE,"E67")])]})]});}
            var Q5;
            Q5=makeQuery(id+"F8.boolean.opBoolean","INTERSECT",EDGE,{"disambiguationData":[OD(0.0)],"derivedFrom":[makeQuery(id+"F5.opExtrude","SWEPT_FACE",FACE,{"disambiguationData":[OSD([sQuery(id+"F4.wireOp",EDGE,"E30")])]}),makeQuery(id+"F8.opExtrude","SWEPT_FACE",FACE,{"disambiguationData":[OSD([sQuery(id+"F7.wireOp",EDGE,"E67")])]})]});
            fillet(context, id + "F14", {"entities" : qUnion([Q0, Q1, Q2, Q3, Q4, Q5]), "radius" : 3 * mm, "tangentPropagation" : true, "allowEdgeOverflow" : false});
        }
        {
            var Q0;
            Q0=makeQuery(id+"F1.opExtrude","CAP_EDGE",EDGE,{"disambiguationData":[OSD([sQuery(id+"F0.wireOp",EDGE,"E1.bottom")])],"isStart":false});
            fillet(context, id + "F15", {"entities" : qUnion([Q0]), "radius" : 2 * mm, "tangentPropagation" : true, "allowEdgeOverflow" : false});
        }
        {
            var Q0;
            {var subQ0=sQuery(id+"F0.wireOp",EDGE,"E21.filletArc");var subQ1=sQuery(id+"F0.wireOp",EDGE,"E7");var subQ2=sQuery(id+"F0.wireOp",EDGE,"E6");var subQ3=sQuery(id+"F0.wireOp",EDGE,"E5");var subQ4=sQuery(id+"F0.wireOp",EDGE,"E4");var subQ5=sQuery(id+"F0.wireOp",EDGE,"E22.filletArc");var subQ6=sQuery(id+"F0.wireOp",EDGE,"E1.bottom");var subQ7=sQuery(id+"F0.wireOp",EDGE,"E1.right");var subQ8=sQuery(id+"F0.wireOp",EDGE,"E1.top");var subQ9=sQuery(id+"F0.wireOp",EDGE,"E1.left");var subQ10=sQuery(id+"F0.wireOp",EDGE,"E23.filletArc");var subQ11=sQuery(id+"F0.wireOp",EDGE,"E24.filletArc");Q0=makeQuery(id+"F2.boolean.opBoolean","SPLIT",FACE,{"disambiguationData":[TD([makeQuery(id+"F1.opExtrude","SWEPT_FACE",FACE,{"disambiguationData":[OSD([subQ6])]})])],"derivedFrom":makeQuery(id+"F1.opExtrude","CAP_FACE",FACE,{"disambiguationData":[OSD([subQ6,subQ8,subQ9,subQ7,subQ4,subQ3,subQ2,subQ1,subQ0,subQ5,subQ10,subQ11])],"isStart":true})});}
            var sketch = newSketch(context, id + "F16", { "sketchPlane" : qUnion([Q0])});
            skArc(sketch, "E79", {"start": v(15, 104.25) * mm, "mid": v(0, 119.25) * mm, "end": v(-15, 104.25) * mm});
            skLineSegment(sketch, "E80", {"start": v(0, 104.25) * mm, "end": v(0, 74.25) * mm, "construction": true});
            skCircle(sketch, "E81", {"center": v(0, 104.25) * mm, "radius": 6 * mm});
            skLineSegment(sketch, "E82", {"start": v(15, 104.25) * mm, "end": v(15, 92.25) * mm});
            skLineSegment(sketch, "E83", {"start": v(-15, 104.25) * mm, "end": v(-15, 92.25) * mm});
            skLineSegment(sketch, "E84", {"start": v(-15, 92.25) * mm, "end": v(-33, 74.25) * mm});
            skLineSegment(sketch, "E85", {"start": v(15, 92.25) * mm, "end": v(33, 74.25) * mm});
            skLineSegment(sketch, "E86", {"start": v(-74.25, 0) * mm, "end": v(74.25, 0) * mm, "construction": true});
            skLineSegment(sketch, "E87.MirrorCS", {"start": v(15, -92.25) * mm, "end": v(33, -74.25) * mm});
            skLineSegment(sketch, "E88.MirrorCS", {"start": v(15, -104.25) * mm, "end": v(15, -92.25) * mm});
            skArc(sketch, "E89.MirrorCS", {"start": v(15, -104.25) * mm, "mid": v(0, -119.25) * mm, "end": v(-15, -104.25) * mm});
            skCircle(sketch, "E90.MirrorC", {"center": v(0, -104.25) * mm, "radius": 6 * mm});
            skLineSegment(sketch, "E91.MirrorCS", {"start": v(-15, -104.25) * mm, "end": v(-15, -92.25) * mm});
            skLineSegment(sketch, "E92.MirrorCS", {"start": v(-15, -92.25) * mm, "end": v(-33, -74.25) * mm});
            skLineSegment(sketch, "E93.MirrorCS", {"start": v(0, -104.25) * mm, "end": v(0, -74.25) * mm, "construction": true});
            skSolve(sketch);
        }
        {
            var Q0;
            Q0 = qSketchRegion(id + "F16", true);
            extrude(context, id + "F17", {"entities" : qUnion([Q0]), "depth" : 25 * mm, "offsetDistance" : 25 * mm});
        }
    });
